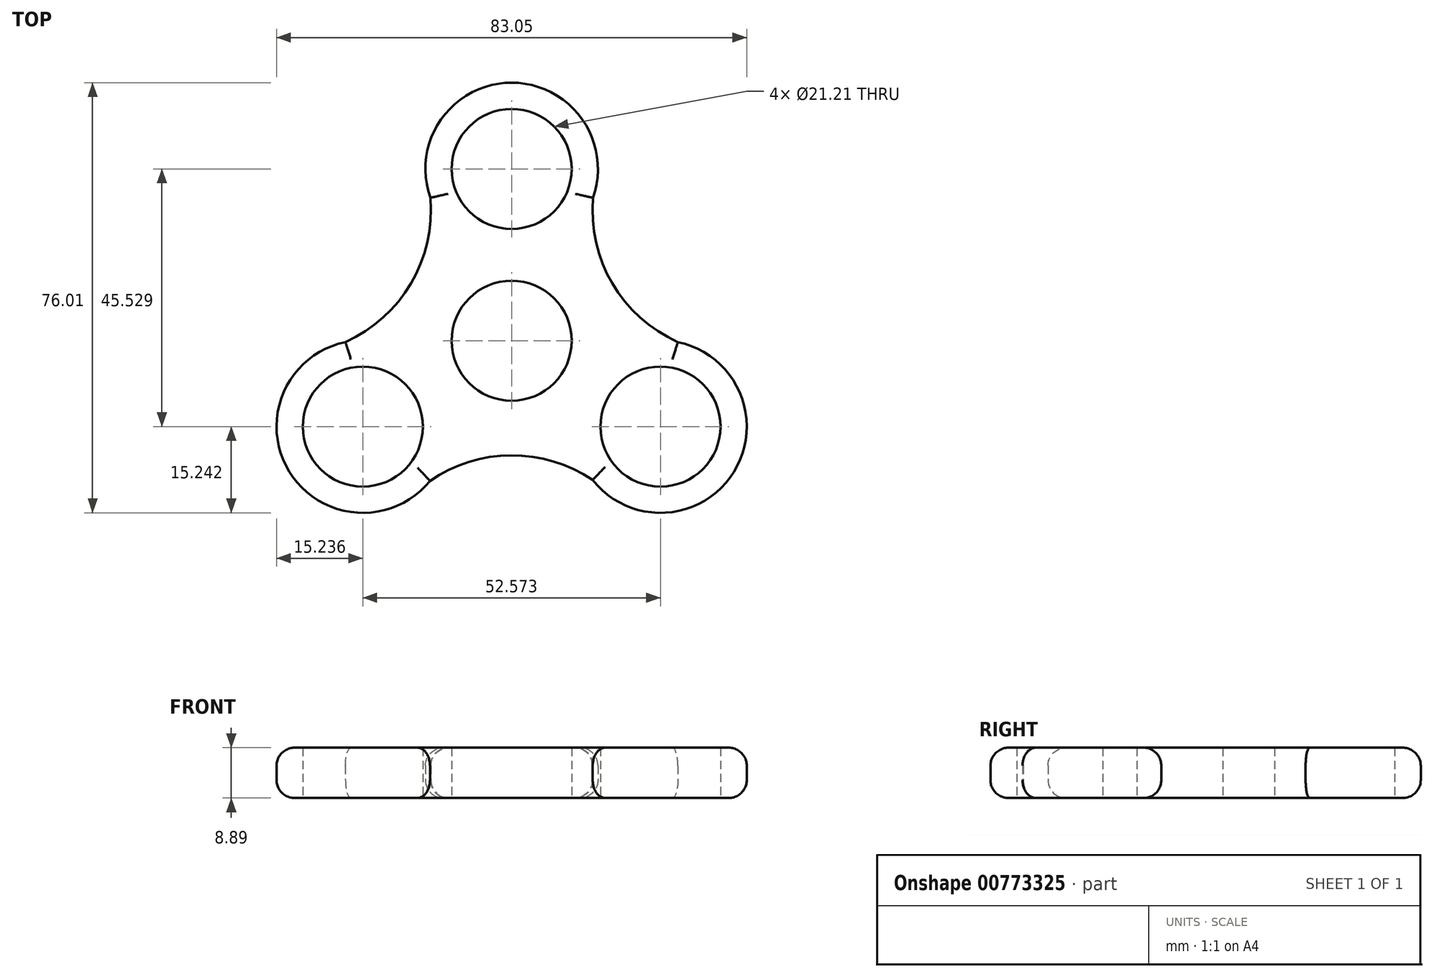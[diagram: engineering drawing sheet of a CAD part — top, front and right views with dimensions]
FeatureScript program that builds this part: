
annotation { "Feature Type Name" : "Feature", "Feature Type Description" : "" }
export const myFeature = defineFeature(function(context is Context, id is Id, definition is map)
    precondition{}
    {
        {
            var Q0;
            Q0=qCreatedBy(makeId("Top.planeOp"),FACE);
            var sketch = newSketch(context, id + "F0", { "sketchPlane" : qUnion([Q0])});
            skCircle(sketch, "E0", {"center": v(37.13, -15.19) * mm, "radius": 10.6 * mm});
            skCircle(sketch, "E1.1.0", {"center": v(63.42, -60.72) * mm, "radius": 10.6 * mm});
            skCircle(sketch, "E1.2.0", {"center": v(10.85, -60.72) * mm, "radius": 10.6 * mm});
            skPoint(sketch, "E1.center", {"position": v(37.13, -45.54) * mm});
            skLineSegment(sketch, "E1.anchor1", {"start": v(37.13, -45.54) * mm, "end": v(37.13, -15.19) * mm, "construction": true});
            skLineSegment(sketch, "E1.anchor2", {"start": v(37.13, -45.54) * mm, "end": v(27.95, -50.84) * mm, "construction": true});
            skCircle(sketch, "E2", {"center": v(37.13, -45.54) * mm, "radius": 10.6 * mm});
            skArc(sketch, "E3", {"start": v(54.1, -71.96) * mm, "mid": v(53.86, -71.75) * mm, "end": v(53.61, -71.54) * mm});
            skPoint(sketch, "E4.orphan", {"position": v(21.9, -15.52) * mm});
            skPoint(sketch, "E5.orphan", {"position": v(52.37, -15.52) * mm});
            skPoint(sketch, "E6.orphan", {"position": v(4.97, -47.35) * mm});
            skPoint(sketch, "E7.orphan", {"position": v(69.3, -47.35) * mm});
            skArc(sketch, "E8", {"start": v(7.78, -45.8) * mm, "mid": v(-2.17, -68.64) * mm, "end": v(22.7, -70.3) * mm});
            skPoint(sketch, "E9.trimOffspring.start.orphan", {"position": v(20.17, -71.96) * mm});
            skArc(sketch, "E10", {"start": v(51.5, -20.28) * mm, "mid": v(37.13, 0.05) * mm, "end": v(22.77, -20.28) * mm});
            skArc(sketch, "E11", {"start": v(51.45, -70.15) * mm, "mid": v(76.39, -68.72) * mm, "end": v(66.5, -45.8) * mm});
            skArc(sketch, "E12", {"start": v(7.78, -45.8) * mm, "mid": v(19.34, -35.43) * mm, "end": v(22.77, -20.28) * mm});
            skArc(sketch, "E13.MirrorCS", {"start": v(66.5, -45.8) * mm, "mid": v(54.93, -35.43) * mm, "end": v(51.5, -20.28) * mm});
            skArc(sketch, "E14", {"start": v(51.45, -70.15) * mm, "mid": v(37.05, -65.8) * mm, "end": v(22.7, -70.3) * mm});
            skLineSegment(sketch, "E15.trimOffspring", {"start": v(24.04, -53.1) * mm, "end": v(10.85, -60.72) * mm, "construction": true});
            skSolve(sketch);
        }
        {
            var Q0;
            Q0=makeQuery(id+"F0.imprint","IMPRINT",FACE,{"disambiguationData":[TD([[makeQuery(id+"F0.imprint","IMPRINT",EDGE,{"derivedFrom":sQuery(id+"F0.wireOp",EDGE,"E0")}),-1.0]])]});
            extrude(context, id + "F1", {"entities" : qUnion([Q0]), "depth" : 8.9 * mm, "offsetDistance" : 25.4 * mm});
        }
        {
            var Q0;
            Q0=makeQuery(id+"F1.opExtrude","CAP_EDGE",EDGE,{"disambiguationData":[OSD([sQuery(id+"F0.wireOp",EDGE,"E14")])],"isStart":false});
            var Q1;
            Q1=makeQuery(id+"F1.opExtrude","CAP_EDGE",EDGE,{"disambiguationData":[OSD([sQuery(id+"F0.wireOp",EDGE,"E8")])],"isStart":false});
            var Q2;
            Q2=makeQuery(id+"F1.opExtrude","CAP_EDGE",EDGE,{"disambiguationData":[OSD([sQuery(id+"F0.wireOp",EDGE,"E12")])],"isStart":false});
            var Q3;
            Q3=makeQuery(id+"F1.opExtrude","CAP_EDGE",EDGE,{"disambiguationData":[OSD([sQuery(id+"F0.wireOp",EDGE,"E10")])],"isStart":false});
            var Q4;
            Q4=makeQuery(id+"F1.opExtrude","CAP_EDGE",EDGE,{"disambiguationData":[OSD([sQuery(id+"F0.wireOp",EDGE,"E13.MirrorCS")])],"isStart":false});
            var Q5;
            Q5=makeQuery(id+"F1.opExtrude","CAP_EDGE",EDGE,{"disambiguationData":[OSD([sQuery(id+"F0.wireOp",EDGE,"E11")])],"isStart":false});
            var Q6;
            Q6=makeQuery(id+"F1.opExtrude","CAP_EDGE",EDGE,{"disambiguationData":[OSD([sQuery(id+"F0.wireOp",EDGE,"E12")])],"isStart":true});
            var Q7;
            Q7=makeQuery(id+"F1.opExtrude","CAP_EDGE",EDGE,{"disambiguationData":[OSD([sQuery(id+"F0.wireOp",EDGE,"E11")])],"isStart":true});
            var Q8;
            Q8=makeQuery(id+"F1.opExtrude","CAP_EDGE",EDGE,{"disambiguationData":[OSD([sQuery(id+"F0.wireOp",EDGE,"E14")])],"isStart":true});
            var Q9;
            Q9=makeQuery(id+"F1.opExtrude","CAP_EDGE",EDGE,{"disambiguationData":[OSD([sQuery(id+"F0.wireOp",EDGE,"E8")])],"isStart":true});
            var Q10;
            Q10=makeQuery(id+"F1.opExtrude","CAP_EDGE",EDGE,{"disambiguationData":[OSD([sQuery(id+"F0.wireOp",EDGE,"E13.MirrorCS")])],"isStart":true});
            var Q11;
            Q11=makeQuery(id+"F1.opExtrude","CAP_EDGE",EDGE,{"disambiguationData":[OSD([sQuery(id+"F0.wireOp",EDGE,"E10")])],"isStart":true});
            fillet(context, id + "F2", {"entities" : qUnion([Q0, Q1, Q2, Q3, Q4, Q5, Q6, Q7, Q8, Q9, Q10, Q11]), "radius" : 3.17 * mm, "tangentPropagation" : true, "allowEdgeOverflow" : false});
        }
    });
